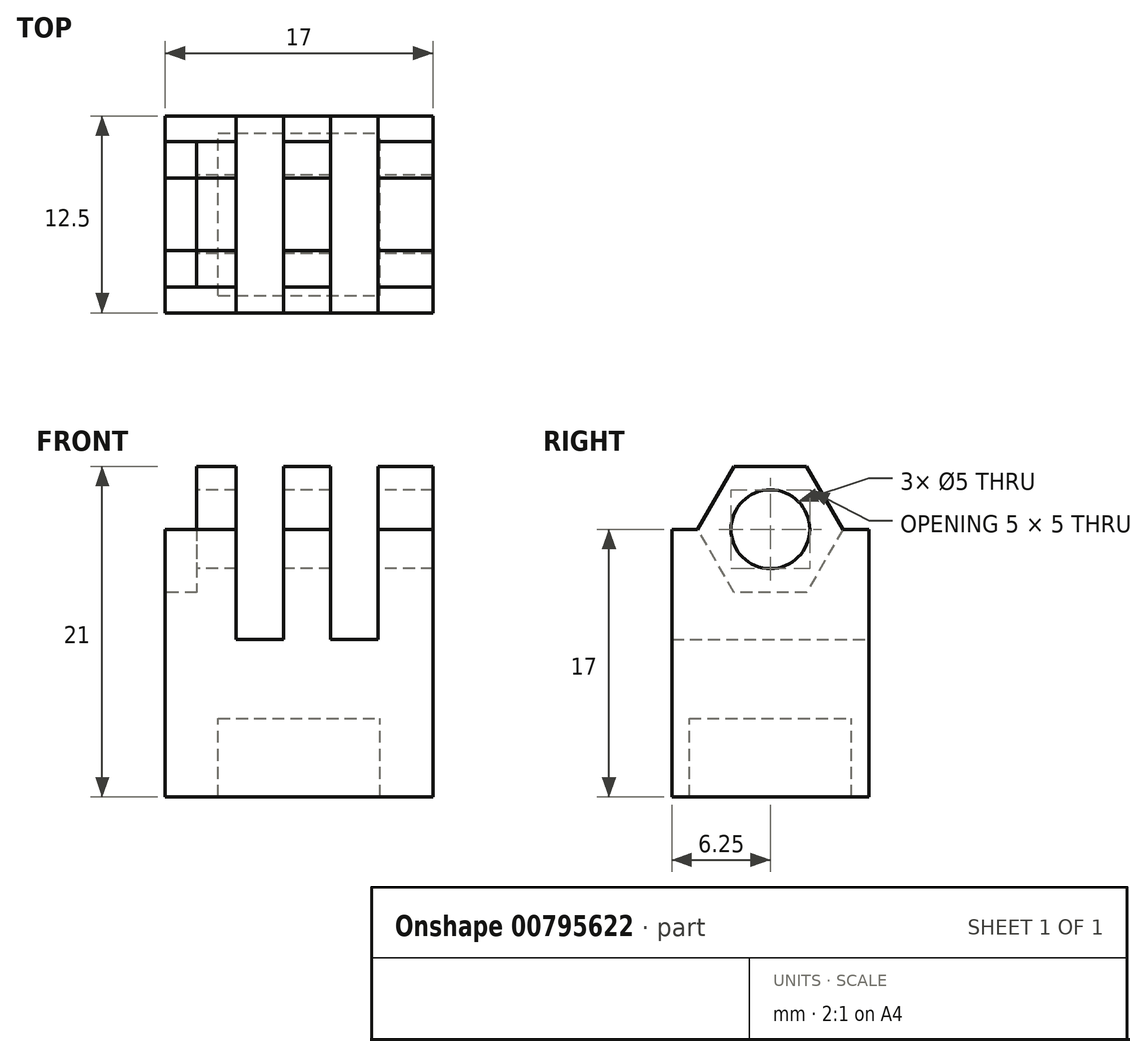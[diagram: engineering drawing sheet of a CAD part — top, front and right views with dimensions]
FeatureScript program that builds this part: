
annotation { "Feature Type Name" : "Feature", "Feature Type Description" : "" }
export const myFeature = defineFeature(function(context is Context, id is Id, definition is map)
    precondition{}
    {
        {
            var Q0;
            Q0=qCreatedBy(makeId("Right.planeOp"),FACE);
            var sketch = newSketch(context, id + "F0", { "sketchPlane" : qUnion([Q0])});
            skLineSegment(sketch, "E0.bottom", {"start": v(-6.25, 0) * mm, "end": v(6.25, 0) * mm});
            skLineSegment(sketch, "E0.top", {"start": v(-6.25, 7) * mm, "end": v(6.25, 7) * mm});
            skLineSegment(sketch, "E0.left", {"start": v(-6.25, 0) * mm, "end": v(-6.25, 7) * mm});
            skLineSegment(sketch, "E0.right", {"start": v(6.25, 0) * mm, "end": v(6.25, 7) * mm});
            skArc(sketch, "E1", {"start": v(-6.25, 7) * mm, "mid": v(0, 13.25) * mm, "end": v(6.25, 7) * mm});
            skCircle(sketch, "E2", {"center": v(0, 7) * mm, "radius": 2.5 * mm});
            skLineSegment(sketch, "E3.top", {"start": v(-6.25, -5) * mm, "end": v(6.25, -5) * mm});
            skLineSegment(sketch, "E3.left", {"start": v(-6.25, 0) * mm, "end": v(-6.25, -5) * mm});
            skLineSegment(sketch, "E3.right", {"start": v(6.25, 0) * mm, "end": v(6.25, -5) * mm});
            skCircle(sketch, "E4.cCircle", {"center": v(0, 7) * mm, "radius": 4 * mm, "construction": true});
            skLineSegment(sketch, "E4.0", {"start": v(2.3, 3) * mm, "end": v(-2.3, 3) * mm});
            skLineSegment(sketch, "E4.1", {"start": v(-2.3, 3) * mm, "end": v(-4.62, 7) * mm});
            skLineSegment(sketch, "E4.2", {"start": v(-4.62, 7) * mm, "end": v(-2.3, 11) * mm});
            skLineSegment(sketch, "E4.3", {"start": v(-2.3, 11) * mm, "end": v(2.3, 11) * mm});
            skLineSegment(sketch, "E4.4", {"start": v(2.3, 11) * mm, "end": v(4.62, 7) * mm});
            skLineSegment(sketch, "E4.5", {"start": v(4.62, 7) * mm, "end": v(2.3, 3) * mm});
            skPoint(sketch, "E4.0.midPoint", {"position": v(0, 3) * mm});
            skSolve(sketch);
        }
        {
            var Q0;
            {var subQ1=sQuery(id+"F0.wireOp",EDGE,"E1");Q0=makeQuery(id+"F0.imprint","IMPRINT",FACE,{"disambiguationData":[TD([[makeQuery(id+"F0.imprint","IMPRINT",EDGE,{"derivedFrom":subQ1}),-1.0]])]});}
            var Q1;
            {var subQ5=sQuery(id+"F0.wireOp",EDGE,"E0.left");Q1=makeQuery(id+"F0.imprint","IMPRINT",FACE,{"disambiguationData":[TD([[makeQuery(id+"F0.imprint","IMPRINT",EDGE,{"derivedFrom":subQ5}),-1.0]])]});}
            var Q2;
            Q2=makeQuery(id+"F0.imprint","IMPRINT",FACE,{"disambiguationData":[TD([[makeQuery(id+"F0.imprint","IMPRINT",EDGE,{"derivedFrom":sQuery(id+"F0.wireOp",EDGE,"E4.0")}),-1.0]])]});
            var Q3;
            {var subQ5=sQuery(id+"F0.wireOp",EDGE,"E4.2");Q3=makeQuery(id+"F0.imprint","IMPRINT",FACE,{"disambiguationData":[TD([[makeQuery(id+"F0.imprint","IMPRINT",EDGE,{"derivedFrom":subQ5}),-1.0]])]});}
            var Q4;
            Q4=makeQuery(id+"F0.imprint","IMPRINT",FACE,{"disambiguationData":[TD([[makeQuery(id+"F0.imprint","IMPRINT",EDGE,{"derivedFrom":sQuery(id+"F0.wireOp",EDGE,"E0.bottom")}),-1.0]])]});
            extrude(context, id + "F1", {"entities" : qUnion([Q0, Q1, Q2, Q3, Q4]), "depth" : 17 * mm, "offsetDistance" : 25 * mm});
        }
        {
            var Q0;
            {var subQ5=sQuery(id+"F0.wireOp",EDGE,"E4.2");Q0=makeQuery(id+"F0.imprint","IMPRINT",FACE,{"disambiguationData":[TD([[makeQuery(id+"F0.imprint","IMPRINT",EDGE,{"derivedFrom":subQ5}),-1.0]])]});}
            var Q1;
            Q1=makeQuery(id+"F0.imprint","IMPRINT",FACE,{"disambiguationData":[TD([[makeQuery(id+"F0.imprint","IMPRINT",EDGE,{"derivedFrom":sQuery(id+"F0.wireOp",EDGE,"E4.0")}),-1.0]])]});
            extrude(context, id + "F2", {"entities" : qUnion([Q0, Q1]), "operationType" : NewBodyOperationType.REMOVE, "depth" : 2 * mm, "offsetDistance" : 25 * mm});
        }
        {
            var Q0;
            Q0=qCreatedBy(makeId("Top.planeOp"),FACE);
            var sketch = newSketch(context, id + "F3", { "sketchPlane" : qUnion([Q0])});
            skLineSegment(sketch, "E5.bottom", {"start": v(4.5, -10.81) * mm, "end": v(7.5, -10.81) * mm});
            skLineSegment(sketch, "E5.top", {"start": v(4.5, 10.01) * mm, "end": v(7.5, 10.01) * mm});
            skLineSegment(sketch, "E5.left", {"start": v(4.5, -10.81) * mm, "end": v(4.5, 10.01) * mm});
            skLineSegment(sketch, "E5.right", {"start": v(7.5, -10.81) * mm, "end": v(7.5, 10.01) * mm});
            skLineSegment(sketch, "E6.bottom", {"start": v(10.5, -11.11) * mm, "end": v(13.5, -11.11) * mm});
            skLineSegment(sketch, "E6.top", {"start": v(10.5, 8.89) * mm, "end": v(13.5, 8.89) * mm});
            skLineSegment(sketch, "E6.left", {"start": v(10.5, -11.11) * mm, "end": v(10.5, 8.89) * mm});
            skLineSegment(sketch, "E6.right", {"start": v(13.5, -11.11) * mm, "end": v(13.5, 8.89) * mm});
            skSolve(sketch);
        }
        {
            var Q0;
            Q0=makeQuery(id+"F3.imprint","IMPRINT",FACE,{"disambiguationData":[TD([[makeQuery(id+"F3.imprint","IMPRINT",EDGE,{"derivedFrom":sQuery(id+"F3.wireOp",EDGE,"E5.bottom")}),1.0]])]});
            var Q1;
            Q1=makeQuery(id+"F3.imprint","IMPRINT",FACE,{"disambiguationData":[TD([[makeQuery(id+"F3.imprint","IMPRINT",EDGE,{"derivedFrom":sQuery(id+"F3.wireOp",EDGE,"E6.bottom")}),1.0]])]});
            extrude(context, id + "F4", {"entities" : qUnion([Q0, Q1]), "operationType" : NewBodyOperationType.REMOVE, "depth" : 25 * mm, "offsetDistance" : 25 * mm});
        }
        {
            var Q0;
            Q0=makeQuery(id+"F1.opExtrude","SWEPT_FACE",FACE,{"disambiguationData":[OSD([sQuery(id+"F0.wireOp",EDGE,"E3.top")])]});
            var sketch = newSketch(context, id + "F5", { "sketchPlane" : qUnion([Q0])});
            skLineSegment(sketch, "E7.bottom", {"start": v(3.35, 5.15) * mm, "end": v(13.65, 5.15) * mm});
            skLineSegment(sketch, "E7.top", {"start": v(3.35, -5.15) * mm, "end": v(13.65, -5.15) * mm});
            skLineSegment(sketch, "E7.left", {"start": v(3.35, 5.15) * mm, "end": v(3.35, -5.15) * mm});
            skLineSegment(sketch, "E7.right", {"start": v(13.65, 5.15) * mm, "end": v(13.65, -5.15) * mm});
            skPoint(sketch, "E8", {"position": v(13.65, 0) * mm});
            skPoint(sketch, "E9", {"position": v(8.5, 5.15) * mm});
            skSolve(sketch);
        }
        {
            var Q0;
            Q0=makeQuery(id+"F5.imprint","IMPRINT",FACE,{"disambiguationData":[TD([[makeQuery(id+"F5.imprint","IMPRINT",EDGE,{"derivedFrom":sQuery(id+"F5.wireOp",EDGE,"E7.bottom")}),1.0]])]});
            extrude(context, id + "F6", {"entities" : qUnion([Q0]), "operationType" : NewBodyOperationType.ADD, "depth" : 5 * mm, "offsetDistance" : 25 * mm});
        }
    });
